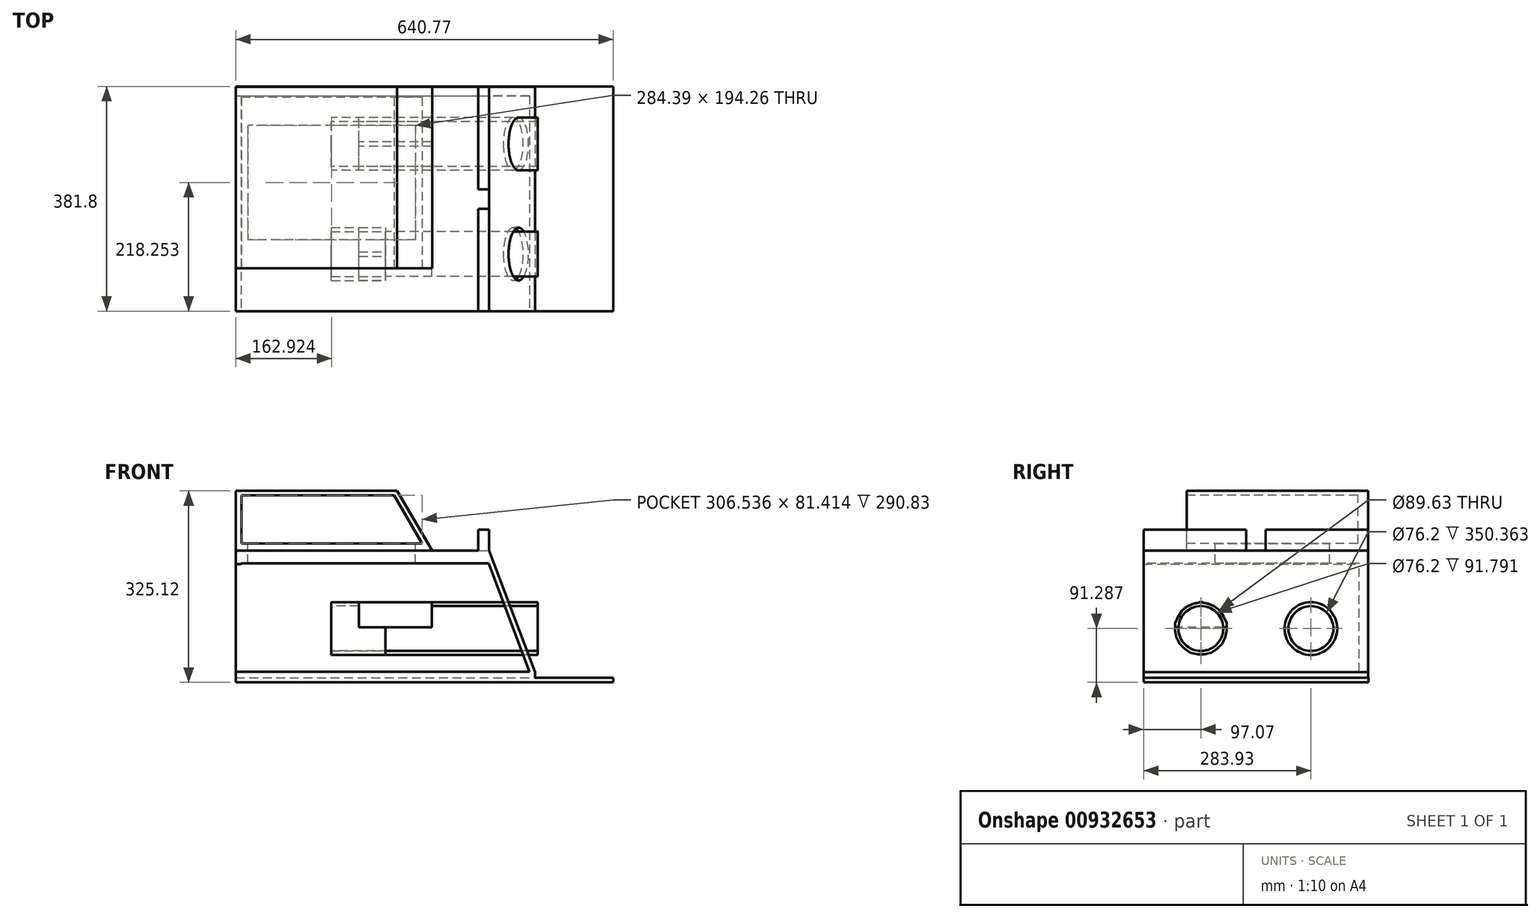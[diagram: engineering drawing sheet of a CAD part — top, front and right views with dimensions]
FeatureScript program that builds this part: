
annotation { "Feature Type Name" : "Feature", "Feature Type Description" : "" }
export const myFeature = defineFeature(function(context is Context, id is Id, definition is map)
    precondition{}
    {
        {
            var Q0;
            Q0=qCreatedBy(makeId("Top.planeOp"),FACE);
            var sketch = newSketch(context, id + "F0", { "sketchPlane" : qUnion([Q0])});
            skLineSegment(sketch, "E0.bottom", {"start": v(-254, -190.5) * mm, "end": v(254, -190.5) * mm});
            skLineSegment(sketch, "E0.top", {"start": v(-254, 190.5) * mm, "end": v(254, 190.5) * mm});
            skLineSegment(sketch, "E0.left", {"start": v(-254, -190.5) * mm, "end": v(-254, 190.5) * mm});
            skLineSegment(sketch, "E0.right", {"start": v(254, -190.5) * mm, "end": v(254, 190.5) * mm});
            skPoint(sketch, "E0.middle", {"position": v(0, 0) * mm});
            skLineSegment(sketch, "E1.bottom", {"start": v(-99.14, -190.5) * mm, "end": v(103.7, -190.5) * mm});
            skLineSegment(sketch, "E1.top", {"start": v(-99.14, 190.5) * mm, "end": v(103.7, 190.5) * mm});
            skLineSegment(sketch, "E1.left", {"start": v(-99.14, -190.5) * mm, "end": v(-99.14, 190.5) * mm});
            skLineSegment(sketch, "E1.right", {"start": v(103.7, -190.5) * mm, "end": v(103.7, 190.5) * mm});
            skPoint(sketch, "E1.middle", {"position": v(2.28, 0) * mm});
            skSolve(sketch);
        }
        {
            var Q0;
            Q0 = qSketchRegion(id + "F0", true);
            extrude(context, id + "F1", {"entities" : qUnion([Q0]), "depth" : 215.9 * mm, "offsetDistance" : 25.4 * mm});
        }
        {
            var Q0;
            Q0=makeQuery(id+"F1.opExtrude","SWEPT_FACE",FACE,{"disambiguationData":[OSD([sQuery(id+"F0.wireOp",EDGE,"E0.bottom"),sQuery(id+"F0.wireOp",EDGE,"E1.bottom")])]});
            var sketch = newSketch(context, id + "F2", { "sketchPlane" : qUnion([Q0])});
            skLineSegment(sketch, "E2.bottom", {"start": v(-244.85, 10.36) * mm, "end": v(244.85, 10.36) * mm});
            skLineSegment(sketch, "E2.top", {"start": v(-244.85, 194.37) * mm, "end": v(244.85, 194.37) * mm});
            skLineSegment(sketch, "E2.left", {"start": v(-244.85, 10.36) * mm, "end": v(-244.85, 194.37) * mm});
            skLineSegment(sketch, "E2.right", {"start": v(244.85, 10.36) * mm, "end": v(244.85, 194.37) * mm});
            skPoint(sketch, "E2.middle", {"position": v(0, 102.37) * mm});
            skLineSegment(sketch, "E3", {"start": v(244.85, 10.36) * mm, "end": v(175.24, 194.37) * mm});
            skLineSegment(sketch, "E4", {"start": v(206.9, 215.9) * mm, "end": v(254, 91.38) * mm});
            skLineSegment(sketch, "E5", {"start": v(254, 9.9) * mm, "end": v(176.07, 215.9) * mm});
            skSolve(sketch);
        }
        {
            var Q0;
            Q0=makeQuery(id+"F2.imprint","IMPRINT",FACE,{"disambiguationData":[TD([[makeQuery(id+"F2.imprint","IMPRINT",EDGE,{"derivedFrom":sQuery(id+"F2.wireOp",EDGE,"E2.bottom")}),1.0]])]});
            extrude(context, id + "F3", {"entities" : qUnion([Q0]), "operationType" : NewBodyOperationType.REMOVE, "oppositeDirection" : true, "depth" : 365.76 * mm, "offsetDistance" : 25.4 * mm});
        }
        {
            var Q0;
            {var subQ0=sQuery(id+"F2.wireOp",EDGE,"E2.right");var subQ1=sQuery(id+"F2.wireOp",EDGE,"E2.top");var subQ2=makeQuery(id+"F2.imprint","INTERSECT",VERTEX,{"derivedFrom":[subQ1,subQ0]});Q0=makeQuery(id+"F2.imprint","IMPRINT",FACE,{"disambiguationData":[TD([[makeQuery(id+"F2.imprint","IMPRINT",EDGE,{"disambiguationData":[TD([[subQ2,1.0]])],"derivedFrom":subQ1}),-1.0]])]});}
            extrude(context, id + "F4", {"entities" : qUnion([Q0]), "operationType" : NewBodyOperationType.REMOVE, "oppositeDirection" : true, "depth" : 474.47 * mm, "offsetDistance" : 25.4 * mm});
        }
        {
            var Q0;
            {var subQ4=sQuery(id+"F2.wireOp",EDGE,"E2.right");var subQ6=sQuery(id+"F2.wireOp",EDGE,"E2.top");var subQ7=makeQuery(id+"F2.imprint","INTERSECT",VERTEX,{"derivedFrom":[subQ6,subQ4]});Q0=makeQuery(id+"F2.imprint","IMPRINT",FACE,{"disambiguationData":[TD([[makeQuery(id+"F2.imprint","IMPRINT",EDGE,{"disambiguationData":[TD([[subQ7,1.0]])],"derivedFrom":subQ6}),1.0]])]});}
            extrude(context, id + "F5", {"entities" : qUnion([Q0]), "operationType" : NewBodyOperationType.REMOVE, "oppositeDirection" : true, "depth" : 384.8 * mm, "offsetDistance" : 25.4 * mm});
        }
        {
            var Q0;
            {var subQ0=sQuery(id+"F2.wireOp",EDGE,"E5");var subQ1=sQuery(id+"F2.wireOp",EDGE,"E2.top");var subQ2=makeQuery(id+"F2.imprint","INTERSECT",VERTEX,{"derivedFrom":[subQ1,subQ0]});Q0=makeQuery(id+"F2.imprint","IMPRINT",FACE,{"disambiguationData":[TD([[makeQuery(id+"F2.imprint","IMPRINT",EDGE,{"disambiguationData":[TD([[subQ2,-1.0]])],"derivedFrom":subQ1}),-1.0]])]});}
            extrude(context, id + "F6", {"entities" : qUnion([Q0]), "operationType" : NewBodyOperationType.REMOVE, "oppositeDirection" : true, "depth" : 463.3 * mm, "offsetDistance" : 25.4 * mm});
        }
        {
            var Q0;
            {var subQ0=sQuery(id+"F2.wireOp",EDGE,"E5");var subQ1=sQuery(id+"F2.wireOp",EDGE,"E2.right");var subQ2=makeQuery(id+"F2.imprint","INTERSECT",VERTEX,{"derivedFrom":[subQ1,subQ0]});Q0=makeQuery(id+"F2.imprint","IMPRINT",FACE,{"disambiguationData":[TD([[makeQuery(id+"F2.imprint","IMPRINT",EDGE,{"disambiguationData":[TD([[subQ2,-1.0]])],"derivedFrom":subQ1}),-1.0]])]});}
            extrude(context, id + "F7", {"entities" : qUnion([Q0]), "operationType" : NewBodyOperationType.REMOVE, "oppositeDirection" : true, "depth" : 453.64 * mm, "offsetDistance" : 25.4 * mm});
        }
        {
            var Q0;
            {var subQ0=sQuery(id+"F2.wireOp",EDGE,"E5");var subQ1=sQuery(id+"F2.wireOp",EDGE,"E2.top");var subQ2=makeQuery(id+"F2.imprint","INTERSECT",VERTEX,{"derivedFrom":[subQ1,subQ0]});Q0=makeQuery(id+"F2.imprint","IMPRINT",FACE,{"disambiguationData":[TD([[makeQuery(id+"F2.imprint","IMPRINT",EDGE,{"disambiguationData":[TD([[subQ2,-1.0]])],"derivedFrom":subQ1}),1.0]])]});}
            extrude(context, id + "F8", {"entities" : qUnion([Q0]), "operationType" : NewBodyOperationType.REMOVE, "oppositeDirection" : true, "depth" : 401.83 * mm, "offsetDistance" : 25.4 * mm});
        }
        {
            var Q0;
            Q0=makeQuery(id+"F1.opExtrude","CAP_FACE",FACE,{"disambiguationData":[OSD([sQuery(id+"F0.wireOp",EDGE,"E0.bottom"),sQuery(id+"F0.wireOp",EDGE,"E0.top"),sQuery(id+"F0.wireOp",EDGE,"E0.left"),sQuery(id+"F0.wireOp",EDGE,"E0.right"),sQuery(id+"F0.wireOp",EDGE,"E1.bottom"),sQuery(id+"F0.wireOp",EDGE,"E1.top")])],"isStart":false});
            var sketch = newSketch(context, id + "F9", { "sketchPlane" : qUnion([Q0])});
            skLineSegment(sketch, "E6.bottom", {"start": v(-254, 190.5) * mm, "end": v(79.33, 190.5) * mm});
            skLineSegment(sketch, "E6.top", {"start": v(-254, -117.66) * mm, "end": v(79.33, -117.66) * mm});
            skLineSegment(sketch, "E6.left", {"start": v(-254, 190.5) * mm, "end": v(-254, -117.66) * mm});
            skLineSegment(sketch, "E6.right", {"start": v(79.33, 190.5) * mm, "end": v(79.33, -117.66) * mm});
            skSolve(sketch);
        }
        {
            var Q0;
            Q0 = qSketchRegion(id + "F9", true);
            extrude(context, id + "F10", {"entities" : qUnion([Q0]), "operationType" : NewBodyOperationType.ADD, "depth" : 101.6 * mm, "offsetDistance" : 25.4 * mm});
        }
        {
            var Q0;
            Q0=makeQuery(id+"F10.opExtrude","SWEPT_FACE",FACE,{"disambiguationData":[OSD([sQuery(id+"F9.wireOp",EDGE,"E6.top")])]});
            var sketch = newSketch(context, id + "F11", { "sketchPlane" : qUnion([Q0])});
            skLineSegment(sketch, "E7", {"start": v(79.33, 215.9) * mm, "end": v(20, 317.5) * mm});
            skLineSegment(sketch, "E8", {"start": v(20, 317.5) * mm, "end": v(0, 317.5) * mm});
            skLineSegment(sketch, "E9", {"start": v(69.42, 215.9) * mm, "end": v(10.1, 317.5) * mm});
            skLineSegment(sketch, "E10.bottom", {"start": v(-244.34, 309.7) * mm, "end": v(62.2, 309.7) * mm});
            skLineSegment(sketch, "E10.top", {"start": v(-244.34, 228.28) * mm, "end": v(62.2, 228.28) * mm});
            skLineSegment(sketch, "E10.left", {"start": v(-244.34, 309.7) * mm, "end": v(-244.34, 228.28) * mm});
            skLineSegment(sketch, "E10.right", {"start": v(62.2, 309.7) * mm, "end": v(62.2, 228.28) * mm});
            skLineSegment(sketch, "E11", {"start": v(79.33, 266.7) * mm, "end": v(-254, 268.99) * mm});
            skPoint(sketch, "E11.endSnap0", {"position": v(62.2, 268.99) * mm});
            skLineSegment(sketch, "E12", {"start": v(-87.34, 317.5) * mm, "end": v(-87.34, 215.9) * mm});
            skSolve(sketch);
        }
        {
            var Q0;
            {var subQ4=sQuery(id+"F11.wireOp",EDGE,"E10.right");var subQ6=sQuery(id+"F11.wireOp",EDGE,"E10.bottom");var subQ7=makeQuery(id+"F11.imprint","INTERSECT",VERTEX,{"derivedFrom":[subQ6,subQ4]});Q0=makeQuery(id+"F11.imprint","IMPRINT",FACE,{"disambiguationData":[TD([[makeQuery(id+"F11.imprint","IMPRINT",EDGE,{"disambiguationData":[TD([[subQ7,1.0]])],"derivedFrom":subQ6}),1.0]])]});}
            var Q1;
            {var subQ0=sQuery(id+"F11.wireOp",EDGE,"E7");var subQ4=sQuery(id+"F11.wireOp",EDGE,"E10.right");var subQ5=makeQuery(id+"F11.imprint","INTERSECT",VERTEX,{"derivedFrom":[subQ0,subQ4]});Q1=makeQuery(id+"F11.imprint","IMPRINT",FACE,{"disambiguationData":[TD([[makeQuery(id+"F11.imprint","IMPRINT",EDGE,{"disambiguationData":[TD([[subQ5,1.0]])],"derivedFrom":subQ4}),1.0]])]});}
            var Q2;
            {var subQ0=sQuery(id+"F11.wireOp",EDGE,"E11");var subQ1=sQuery(id+"F11.wireOp",EDGE,"E7");var subQ2=makeQuery(id+"F11.imprint","INTERSECT",VERTEX,{"derivedFrom":[subQ1,subQ0]});Q2=makeQuery(id+"F11.imprint","IMPRINT",FACE,{"disambiguationData":[TD([[makeQuery(id+"F11.imprint","IMPRINT",EDGE,{"disambiguationData":[TD([[subQ2,-1.0]])],"derivedFrom":subQ1}),-1.0]])]});}
            var Q3;
            {var subQ0=sQuery(id+"F11.wireOp",EDGE,"E10.right");var subQ1=sQuery(id+"F11.wireOp",EDGE,"E7");var subQ2=makeQuery(id+"F11.imprint","INTERSECT",VERTEX,{"derivedFrom":[subQ1,subQ0]});Q3=makeQuery(id+"F11.imprint","IMPRINT",FACE,{"disambiguationData":[TD([[makeQuery(id+"F11.imprint","IMPRINT",EDGE,{"disambiguationData":[TD([[subQ2,-1.0]])],"derivedFrom":subQ1}),-1.0]])]});}
            extrude(context, id + "F12", {"entities" : qUnion([Q0, Q1, Q2, Q3]), "operationType" : NewBodyOperationType.REMOVE, "oppositeDirection" : true, "depth" : 332.74 * mm, "offsetDistance" : 25.4 * mm});
        }
        {
            var Q0;
            {var subQ0=sQuery(id+"F11.wireOp",EDGE,"E11");var subQ1=sQuery(id+"F11.wireOp",EDGE,"E9");var subQ2=makeQuery(id+"F11.imprint","INTERSECT",VERTEX,{"derivedFrom":[subQ1,subQ0]});Q0=makeQuery(id+"F11.imprint","IMPRINT",FACE,{"disambiguationData":[TD([[makeQuery(id+"F11.imprint","IMPRINT",EDGE,{"disambiguationData":[TD([[subQ2,-1.0]])],"derivedFrom":subQ1}),1.0]])]});}
            var Q1;
            {var subQ0=sQuery(id+"F11.wireOp",EDGE,"E10.left");var subQ1=sQuery(id+"F11.wireOp",EDGE,"E10.bottom");var subQ2=makeQuery(id+"F11.imprint","INTERSECT",VERTEX,{"derivedFrom":[subQ1,subQ0]});Q1=makeQuery(id+"F11.imprint","IMPRINT",FACE,{"disambiguationData":[TD([[makeQuery(id+"F11.imprint","IMPRINT",EDGE,{"disambiguationData":[TD([[subQ2,-1.0]])],"derivedFrom":subQ1}),-1.0]])]});}
            var Q2;
            {var subQ1=sQuery(id+"F11.wireOp",EDGE,"E9");var subQ3=sQuery(id+"F11.wireOp",EDGE,"E11");var subQ4=makeQuery(id+"F11.imprint","INTERSECT",VERTEX,{"derivedFrom":[subQ1,subQ3]});Q2=makeQuery(id+"F11.imprint","IMPRINT",FACE,{"disambiguationData":[TD([[makeQuery(id+"F11.imprint","IMPRINT",EDGE,{"disambiguationData":[TD([[subQ4,-1.0]])],"derivedFrom":subQ3}),1.0]])]});}
            var Q3;
            {var subQ0=sQuery(id+"F11.wireOp",EDGE,"E10.left");var subQ1=sQuery(id+"F11.wireOp",EDGE,"E10.top");var subQ2=makeQuery(id+"F11.imprint","INTERSECT",VERTEX,{"derivedFrom":[subQ1,subQ0]});Q3=makeQuery(id+"F11.imprint","IMPRINT",FACE,{"disambiguationData":[TD([[makeQuery(id+"F11.imprint","IMPRINT",EDGE,{"disambiguationData":[TD([[subQ2,-1.0]])],"derivedFrom":subQ1}),1.0]])]});}
            extrude(context, id + "F13", {"entities" : qUnion([Q0, Q1, Q2, Q3]), "operationType" : NewBodyOperationType.REMOVE, "oppositeDirection" : true, "depth" : 290.83 * mm, "offsetDistance" : 25.4 * mm});
        }
        {
            var Q0;
            Q0=makeQuery(id+"F1.opExtrude","CAP_FACE",FACE,{"disambiguationData":[OSD([sQuery(id+"F0.wireOp",EDGE,"E0.bottom"),sQuery(id+"F0.wireOp",EDGE,"E0.top"),sQuery(id+"F0.wireOp",EDGE,"E0.left"),sQuery(id+"F0.wireOp",EDGE,"E0.right"),sQuery(id+"F0.wireOp",EDGE,"E1.bottom"),sQuery(id+"F0.wireOp",EDGE,"E1.top")])],"isStart":true});
            var sketch = newSketch(context, id + "F14", { "sketchPlane" : qUnion([Q0])});
            skLineSegment(sketch, "E13.bottom", {"start": v(-254, 190.5) * mm, "end": v(386.77, 190.5) * mm});
            skLineSegment(sketch, "E13.top", {"start": v(-254, -191.3) * mm, "end": v(386.77, -191.3) * mm});
            skLineSegment(sketch, "E13.left", {"start": v(-254, 190.5) * mm, "end": v(-254, -191.3) * mm});
            skLineSegment(sketch, "E13.right", {"start": v(386.77, 190.5) * mm, "end": v(386.77, -191.3) * mm});
            skSolve(sketch);
        }
        {
            var Q0;
            Q0 = qSketchRegion(id + "F14", true);
            extrude(context, id + "F15", {"entities" : qUnion([Q0]), "operationType" : NewBodyOperationType.ADD, "depth" : 7.62 * mm, "offsetDistance" : 25.4 * mm});
        }
        {
            var Q0;
            Q0=makeQuery(id+"F1.opExtrude","CAP_FACE",FACE,{"disambiguationData":[OSD([sQuery(id+"F0.wireOp",EDGE,"E0.bottom"),sQuery(id+"F0.wireOp",EDGE,"E0.top"),sQuery(id+"F0.wireOp",EDGE,"E0.left"),sQuery(id+"F0.wireOp",EDGE,"E0.right"),sQuery(id+"F0.wireOp",EDGE,"E1.bottom"),sQuery(id+"F0.wireOp",EDGE,"E1.top")])],"isStart":false});
            var sketch = newSketch(context, id + "F16", { "sketchPlane" : qUnion([Q0])});
            skLineSegment(sketch, "E14.bottom", {"start": v(176.07, 190.5) * mm, "end": v(157.62, 190.5) * mm});
            skLineSegment(sketch, "E14.top", {"start": v(176.07, -190.5) * mm, "end": v(157.62, -190.5) * mm});
            skLineSegment(sketch, "E14.left", {"start": v(176.07, 190.5) * mm, "end": v(176.07, -190.5) * mm});
            skLineSegment(sketch, "E14.right", {"start": v(157.62, 190.5) * mm, "end": v(157.62, -190.5) * mm});
            skLineSegment(sketch, "E15.bottom", {"start": v(157.62, -16.32) * mm, "end": v(194.52, -16.32) * mm});
            skLineSegment(sketch, "E15.top", {"start": v(157.62, 16.32) * mm, "end": v(194.52, 16.32) * mm});
            skLineSegment(sketch, "E15.left", {"start": v(157.62, -16.32) * mm, "end": v(157.62, 16.32) * mm});
            skLineSegment(sketch, "E15.right", {"start": v(194.52, -16.32) * mm, "end": v(194.52, 16.32) * mm});
            skPoint(sketch, "E15.middle", {"position": v(176.07, 0) * mm});
            skSolve(sketch);
        }
        {
            var Q0;
            {var subQ0=sQuery(id+"F16.wireOp",EDGE,"E14.bottom");Q0=makeQuery(id+"F16.imprint","IMPRINT",FACE,{"disambiguationData":[TD([[makeQuery(id+"F16.imprint","IMPRINT",EDGE,{"derivedFrom":subQ0}),-1.0]])]});}
            var Q1;
            {var subQ5=sQuery(id+"F16.wireOp",EDGE,"E15.left");Q1=makeQuery(id+"F16.imprint","IMPRINT",FACE,{"disambiguationData":[TD([[makeQuery(id+"F16.imprint","IMPRINT",EDGE,{"derivedFrom":subQ5}),-1.0]])]});}
            var Q2;
            {var subQ0=sQuery(id+"F16.wireOp",EDGE,"E14.top");Q2=makeQuery(id+"F16.imprint","IMPRINT",FACE,{"disambiguationData":[TD([[makeQuery(id+"F16.imprint","IMPRINT",EDGE,{"derivedFrom":subQ0}),1.0]])]});}
            extrude(context, id + "F17", {"entities" : qUnion([Q0, Q1, Q2]), "operationType" : NewBodyOperationType.ADD, "depth" : 35.56 * mm, "offsetDistance" : 25.4 * mm});
        }
        {
            var Q0;
            Q0=qCreatedBy(makeId("Right.planeOp"),FACE);
            var sketch = newSketch(context, id + "F18", { "sketchPlane" : qUnion([Q0])});
            skLineSegment(sketch, "E16", {"start": v(0, 0) * mm, "end": v(0, 213.5) * mm});
            skLineSegment(sketch, "E17", {"start": v(0, 213.5) * mm, "end": v(0, -66.07) * mm});
            skLineSegment(sketch, "E18", {"start": v(221.54, 83.67) * mm, "end": v(221.54, 201.44) * mm});
            skLineSegment(sketch, "E19.MirrorCS", {"start": v(0, 167.33) * mm, "end": v(0, -46.16) * mm});
            skCircle(sketch, "E20", {"center": v(93.43, 83.67) * mm, "radius": 38.1 * mm});
            skCircle(sketch, "E21.MirrorC", {"center": v(-93.43, 83.67) * mm, "radius": 38.1 * mm});
            skCircle(sketch, "E22", {"center": v(-93.43, 83.67) * mm, "radius": 44.82 * mm});
            skCircle(sketch, "E23.MirrorC", {"center": v(93.43, 83.67) * mm, "radius": 44.82 * mm});
            skSolve(sketch);
        }
        {
            var Q0;
            Q0=makeQuery(id+"F18.imprint","IMPRINT",FACE,{"disambiguationData":[TD([[makeQuery(id+"F18.imprint","IMPRINT",EDGE,{"derivedFrom":sQuery(id+"F18.wireOp",EDGE,"E21.MirrorC")}),1.0]])]});
            var Q1;
            Q1=sQuery(id+"F18.wireOp",EDGE,"E22");
            var Q2;
            Q2=sQuery(id+"F18.wireOp",EDGE,"E23.MirrorC");
            extrude(context, id + "F19", {"entities" : qUnion([Q0]), "operationType" : NewBodyOperationType.ADD, "surfaceEntities" : qUnion([Q1, Q2]), "depth" : 258.57 * mm, "offsetDistance" : 25.4 * mm});
        }
        {
            var Q0;
            Q0=makeQuery(id+"F18.imprint","IMPRINT",FACE,{"disambiguationData":[TD([[makeQuery(id+"F18.imprint","IMPRINT",EDGE,{"derivedFrom":sQuery(id+"F18.wireOp",EDGE,"E21.MirrorC")}),-1.0]])]});
            extrude(context, id + "F20", {"entities" : qUnion([Q0]), "operationType" : NewBodyOperationType.REMOVE, "depth" : 485.14 * mm, "offsetDistance" : 25.4 * mm});
        }
        {
            var Q0;
            Q0=makeQuery(id+"F18.imprint","IMPRINT",FACE,{"disambiguationData":[TD([[makeQuery(id+"F18.imprint","IMPRINT",EDGE,{"derivedFrom":sQuery(id+"F18.wireOp",EDGE,"E20")}),-1.0]])]});
            var Q1;
            Q1=makeQuery(id+"F18.imprint","IMPRINT",FACE,{"disambiguationData":[TD([[makeQuery(id+"F18.imprint","IMPRINT",EDGE,{"derivedFrom":sQuery(id+"F18.wireOp",EDGE,"E21.MirrorC")}),1.0]])]});
            extrude(context, id + "F21", {"entities" : qUnion([Q0, Q1]), "operationType" : NewBodyOperationType.ADD, "depth" : 258.57 * mm, "offsetDistance" : 25.4 * mm});
        }
        {
            var Q0;
            Q0 = qSketchRegion(id + "F18", true);
            extrude(context, id + "F22", {"entities" : qUnion([Q0]), "operationType" : NewBodyOperationType.REMOVE, "oppositeDirection" : true, "depth" : 57.66 * mm, "offsetDistance" : 25.4 * mm});
        }
        {
            var Q0;
            Q0 = qSketchRegion(id + "F18", true);
            var Q1;
            {var subQ0=sQuery(id+"F2.wireOp",EDGE,"E5");Q1=makeQuery(id+"F21.boolean.opBoolean","SPLIT",FACE,{"disambiguationData":[TD([makeQuery(id+"F21.opExtrude","SWEPT_FACE",FACE,{"disambiguationData":[OSD([sQuery(id+"F18.wireOp",EDGE,"E20")])]})])],"derivedFrom":makeQuery(id+"F19.boolean.opBoolean","SPLIT",FACE,{"disambiguationData":[TD([makeQuery(id+"F1.opExtrude","SWEPT_FACE",FACE,{"disambiguationData":[OSD([sQuery(id+"F0.wireOp",EDGE,"E0.right")])]})])],"derivedFrom":makeQuery(id+"F8.boolean.opBoolean","MERGE",FACE,{"derivedFrom":[makeQuery(id+"F7.boolean.opBoolean","MERGE",FACE,{"derivedFrom":[makeQuery(id+"F6.boolean.opBoolean","COPY",FACE,{"derivedFrom":makeQuery(id+"F6.opExtrude","SWEPT_FACE",FACE,{"disambiguationData":[OSD([subQ0])]})})],"fromTools":[makeQuery(id+"F7.opExtrude","SWEPT_FACE",FACE,{"disambiguationData":[OSD([subQ0])]})]})],"fromTools":[makeQuery(id+"F8.opExtrude","SWEPT_FACE",FACE,{"disambiguationData":[OSD([subQ0])]})]})})});}
            extrude(context, id + "F23", {"entities" : qUnion([Q0, Q1]), "operationType" : NewBodyOperationType.REMOVE, "oppositeDirection" : true, "depth" : 72.9 * mm, "offsetDistance" : 25.4 * mm});
        }
        {
            var Q0;
            Q0 = qSketchRegion(id + "F18", true);
            extrude(context, id + "F24", {"entities" : qUnion([Q0]), "operationType" : NewBodyOperationType.ADD, "oppositeDirection" : true, "depth" : 250.2 * mm, "offsetDistance" : 25.4 * mm});
        }
        {
            var Q0;
            Q0=makeQuery(id+"F13.boolean.opBoolean","COPY",FACE,{"derivedFrom":makeQuery(id+"F13.opExtrude","SWEPT_FACE",FACE,{"disambiguationData":[OSD([sQuery(id+"F11.wireOp",EDGE,"E10.top")])]})});
            var sketch = newSketch(context, id + "F25", { "sketchPlane" : qUnion([Q0])});
            skLineSegment(sketch, "E24", {"start": v(-91.08, -117.66) * mm, "end": v(-91.08, 299.18) * mm});
            skLineSegment(sketch, "E25", {"start": v(62.2, 0) * mm, "end": v(62.2, 27.75) * mm});
            skLineSegment(sketch, "E26", {"start": v(62.2, 27.75) * mm, "end": v(-244.34, 27.75) * mm});
            skLineSegment(sketch, "E27.bottom", {"start": v(-233.27, -69.37) * mm, "end": v(51.12, -69.37) * mm});
            skLineSegment(sketch, "E27.top", {"start": v(-233.27, 124.88) * mm, "end": v(51.12, 124.88) * mm});
            skLineSegment(sketch, "E27.left", {"start": v(-233.27, -69.37) * mm, "end": v(-233.27, 124.88) * mm});
            skLineSegment(sketch, "E27.right", {"start": v(51.12, -69.37) * mm, "end": v(51.12, 124.88) * mm});
            skPoint(sketch, "E27.middle", {"position": v(-91.08, 27.75) * mm});
            skSolve(sketch);
        }
        {
            var Q0;
            Q0 = qSketchRegion(id + "F25", true);
            extrude(context, id + "F26", {"entities" : qUnion([Q0]), "operationType" : NewBodyOperationType.REMOVE, "oppositeDirection" : true, "depth" : 68.58 * mm, "offsetDistance" : 25.4 * mm});
        }
        {
            var Q0;
            Q0=makeQuery(id+"F3.boolean.opBoolean","COPY",FACE,{"derivedFrom":makeQuery(id+"F3.opExtrude","CAP_FACE",FACE,{"disambiguationData":[OSD([sQuery(id+"F2.wireOp",EDGE,"E2.bottom"),sQuery(id+"F2.wireOp",EDGE,"E2.top"),sQuery(id+"F2.wireOp",EDGE,"E2.left"),sQuery(id+"F2.wireOp",EDGE,"E3")])],"isStart":false})});
            var sketch = newSketch(context, id + "F27", { "sketchPlane" : qUnion([Q0])});
            skLineSegment(sketch, "E28", {"start": v(-168.43, 194.37) * mm, "end": v(-45, 85.96) * mm});
            skLineSegment(sketch, "E29", {"start": v(-45, 85.96) * mm, "end": v(79.16, 85.96) * mm});
            skLineSegment(sketch, "E30", {"start": v(79.16, 85.96) * mm, "end": v(79.16, 121.75) * mm});
            skLineSegment(sketch, "E31.top", {"start": v(-45, 128.32) * mm, "end": v(79.16, 128.32) * mm});
            skLineSegment(sketch, "E31.left", {"start": v(-45, 85.96) * mm, "end": v(-45, 128.32) * mm});
            skLineSegment(sketch, "E31.right", {"start": v(79.16, 85.96) * mm, "end": v(79.16, 128.32) * mm});
            skSolve(sketch);
        }
        {
            var Q0;
            Q0 = qSketchRegion(id + "F27", true);
            extrude(context, id + "F28", {"entities" : qUnion([Q0]), "operationType" : NewBodyOperationType.REMOVE, "depth" : 340.87 * mm, "offsetDistance" : 25.4 * mm});
        }
        {
            var Q0;
            Q0=sQuery(id+"F27.wireOp",EDGE,"E28");
            extrude(context, id + "F29", {"bodyType" : ToolBodyType.SURFACE, "surfaceEntities" : qUnion([Q0]), "depth" : 344.68 * mm, "offsetDistance" : 25.4 * mm});
        }
        {
            var Q0;
            Q0=makeQuery(id+"F3.boolean.opBoolean","COPY",FACE,{"derivedFrom":makeQuery(id+"F3.opExtrude","CAP_FACE",FACE,{"disambiguationData":[OSD([sQuery(id+"F2.wireOp",EDGE,"E2.bottom"),sQuery(id+"F2.wireOp",EDGE,"E2.top"),sQuery(id+"F2.wireOp",EDGE,"E2.left"),sQuery(id+"F2.wireOp",EDGE,"E3")])],"isStart":false})});
            var sketch = newSketch(context, id + "F30", { "sketchPlane" : qUnion([Q0])});
            skLineSegment(sketch, "E32.bottom", {"start": v(-269.43, 193.06) * mm, "end": v(-91.8, 193.06) * mm});
            skLineSegment(sketch, "E32.top", {"start": v(-269.43, 10.36) * mm, "end": v(-91.8, 10.36) * mm});
            skLineSegment(sketch, "E32.left", {"start": v(-269.43, 193.06) * mm, "end": v(-269.43, 10.36) * mm});
            skLineSegment(sketch, "E32.right", {"start": v(-91.8, 193.06) * mm, "end": v(-91.8, 10.36) * mm});
            skSolve(sketch);
        }
        {
            var Q0;
            Q0 = qSketchRegion(id + "F30", true);
            extrude(context, id + "F31", {"entities" : qUnion([Q0]), "operationType" : NewBodyOperationType.REMOVE, "depth" : 723.9 * mm, "offsetDistance" : 25.4 * mm});
        }
    });
